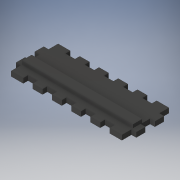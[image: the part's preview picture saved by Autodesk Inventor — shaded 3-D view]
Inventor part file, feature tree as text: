
AUTODESK INVENTOR PART (.ipt)
format: ipt  version: 2019 (Build 230136000, 136)  size: 207,360 bytes
history: native  units: mm
features: extrude x3, sketch x3, projected_geometry x1
ambient origin geometry x8: Origin, YZ Plane, XZ Plane, XY Plane, X Axis, Y Axis, Z Axis, Center Point
bodies: Solid1 (feature_tree)
feature tree (7):
  extrude  "Extrusion1"  Depth=39.0mm
  extrude  "Extrusion2"  Depth=4.0mm
  extrude  "Extrusion3"  Depth=8.0mm
  sketch  "Sketch1"  dims[d0=100.0mm d1=39.0mm]
  sketch  "Sketch2"  dims[d2=4.0mm d3=0.0mm d4=4.0mm]
  projected_geometry  "Projected Loop1"
  sketch  "Sketch3"  dims[d5=4.0mm d7=8.0mm d8=8.0mm d10=8.0mm d11=8.0mm d13=4.0mm d14=8.0mm d15=4.0mm d16=0.0mm d17=5.0mm d18=8.0mm d19=3.0mm d20=0.0mm]
